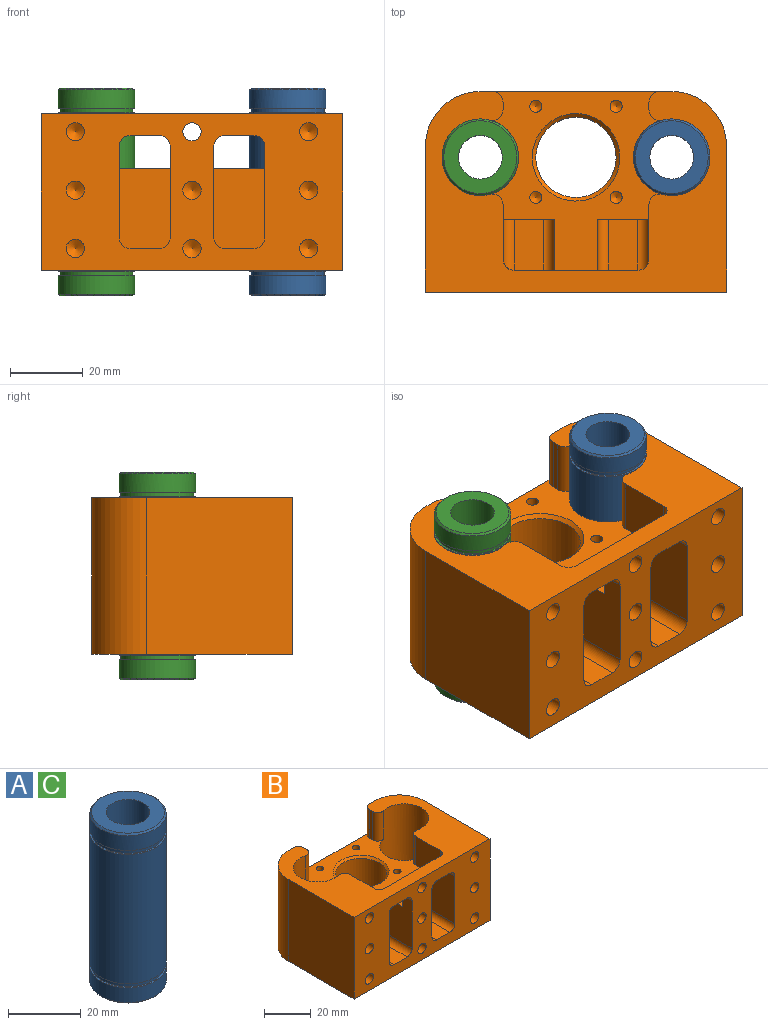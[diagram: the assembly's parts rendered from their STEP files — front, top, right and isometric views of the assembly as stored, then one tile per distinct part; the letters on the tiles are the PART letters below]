
ASSEMBLY  parts=3 mates=2
PART A: 14 faces, bbox 21x21x57 mm
  f0: cylinder r=6mm len=57mm, axis (0,0,1), area 2148.8mm2, adj f1,f7
  f1: plane 20x20mm, normal (0,0,-1), area 201.1mm2, adj f0,f12
  f2: cylinder r=10.5mm len=21mm, axis (0,0,1), area 329.9mm2, adj f3,f12
  f3: plane 21x21mm, normal (0,0,1), area 32.2mm2, adj f2,f4
  f4: cylinder r=10mm len=20mm, axis (0,0,1), area 81.7mm2, adj f3,f5
  f5: plane 21x21mm, normal (0,0,-1), area 32.2mm2, adj f4,f6
  f6: cylinder r=10.5mm len=43.4mm, axis (0,0,1), area 2863.2mm2, adj f5,f11
  f7: plane 20x20mm, normal (0,0,1), area 201.1mm2, adj f0,f13
  f8: cylinder r=10.5mm len=21mm, axis (0,0,-1), area 329.9mm2, adj f9,f13
  f9: plane 21x21mm, normal (0,0,-1), area 32.2mm2, adj f8,f10
  f10: cylinder r=10mm len=20mm, axis (0,0,-1), area 81.7mm2, adj f9,f11
  f11: plane 21x21mm, normal (0,0,1), area 32.2mm2, adj f6,f10
  f12: cone r=10.5mm half-angle=45deg, axis (0,0,1), area 45.5mm2, adj f1,f2
  f13: cone r=10mm half-angle=45deg, axis (0,0,-1), area 45.5mm2, adj f7,f8
PART B: 67 faces, bbox 82.6x55x43 mm
  f0: plane 82.6x43mm, normal (0,-1,0), area 2522.5mm2, adj f5,f6,f7,f9,f12,f14,f35,f37
  f1: plane 49x47.44mm, normal (0,0,1), area 1002.3mm2, adj f2,f4,f8,f9,f10,f13,f14,f15
  f2: plane 34x15mm, normal (0,1,0), area 296.2mm2, adj f1,f3,f6,f26,f48,f51,f53,f58
  f3: cylinder r=3mm len=9mm, axis (0,0,1), area 33.4mm2, adj f2,f6,f9,f55
  f4: plane 52.6x43mm, normal (0,1,0), area 1571.8mm2, adj f1,f6,f7,f11,f16,f29,f30
  f5: plane 43x40mm, normal (-1,0,0), area 1720mm2, adj f0,f6,f7,f11
  f6: plane 82.6x55mm, normal (0,0,1), area 1876.7mm2, adj f0,f2,f3,f4,f5,f8,f9,f10
  f7: plane 82.6x55mm, normal (0,0,-1), area 3373.6mm2, adj f0,f4,f5,f8,f11,f12,f13,f16
  f8: cylinder r=10.5mm len=43mm, axis (0,0,1), area 2418.6mm2, adj f1,f6,f7,f31,f32
  f9: plane 34x23.9mm, normal (1,0,0), area 657.5mm2, adj f0,f1,f3,f6,f31,f54,f55,f56
  f10: plane 15x1.9mm, normal (1,0,0), area 28.5mm2, adj f1,f6,f30,f32
  f11: cylinder r=15mm len=43mm, axis (0,0,1), area 1013.2mm2, adj f4,f5,f6,f7
  f12: plane 43x40mm, normal (1,0,0), area 1720mm2, adj f0,f6,f7,f16
  f13: cylinder r=10.5mm len=43mm, axis (0,0,1), area 2418.6mm2, adj f1,f6,f7,f27,f28
  f14: plane 34x23.9mm, normal (-1,0,0), area 657.5mm2, adj f0,f1,f6,f26,f27,f62,f63,f64
  f15: plane 15x1.9mm, normal (-1,0,0), area 28.5mm2, adj f1,f6,f28,f29
  f16: cylinder r=15mm len=43mm, axis (0,0,1), area 1013.2mm2, adj f4,f6,f7,f12
  f17: cylinder r=11mm len=27mm, axis (0,0,1), area 1866.1mm2, adj f7,f33
  f18: cone r=0mm half-angle=59deg, axis (0,0,1), area 10mm2, adj f19
  f19: cylinder r=1.65mm len=14.1mm, axis (0,0,1), area 146.2mm2, adj f1,f18
  f20: cone r=0mm half-angle=59deg, axis (0,0,1), area 10mm2, adj f21
  f21: cylinder r=1.65mm len=14.1mm, axis (0,0,1), area 146.2mm2, adj f1,f20
  f22: cone r=0mm half-angle=59deg, axis (0,0,1), area 10mm2, adj f23
  f23: cylinder r=1.65mm len=14.1mm, axis (0,0,1), area 146.2mm2, adj f1,f22
  f24: cone r=0mm half-angle=59deg, axis (0,0,1), area 10mm2, adj f25
  f25: cylinder r=1.65mm len=14.1mm, axis (0,0,1), area 146.2mm2, adj f1,f24
  f26: cylinder r=3mm len=9mm, axis (0,0,1), area 33.4mm2, adj f2,f6,f14,f63
  f27: cylinder r=3mm len=15mm, axis (0,0,1), area 81.6mm2, adj f1,f6,f13,f14
  f28: cylinder r=3mm len=15mm, axis (0,0,1), area 81.6mm2, adj f1,f6,f13,f15
  f29: cylinder r=3mm len=15mm, axis (0,0,-1), area 70.7mm2, adj f1,f4,f6,f15
  f30: cylinder r=3mm len=15mm, axis (0,0,-1), area 70.7mm2, adj f1,f4,f6,f10
  f31: cylinder r=3mm len=15mm, axis (0,0,1), area 81.6mm2, adj f1,f6,f8,f9
  f32: cylinder r=3mm len=15mm, axis (0,0,1), area 81.6mm2, adj f1,f6,f8,f10
  f33: cone r=11mm half-angle=45deg, axis (0,0,1), area 102.2mm2, adj f1,f17
  f34: cone r=0mm half-angle=59deg, axis (0,-1,0), area 22.9mm2, adj f35
  f35: cylinder r=2.5mm len=15mm, axis (0,-1,0), area 235.6mm2, adj f0,f34
  f36: cone r=0mm half-angle=59deg, axis (0,-1,0), area 22.9mm2, adj f37
  f37: cylinder r=2.5mm len=15mm, axis (0,-1,0), area 235.6mm2, adj f0,f36
  f38: cone r=0mm half-angle=59deg, axis (0,-1,0), area 22.9mm2, adj f39
  f39: cylinder r=2.5mm len=15mm, axis (0,-1,0), area 235.6mm2, adj f0,f38
  f40: cone r=0mm half-angle=59deg, axis (0,-1,0), area 22.9mm2, adj f41
  f41: cylinder r=2.5mm len=15mm, axis (0,-1,0), area 235.6mm2, adj f0,f40
  f42: cone r=0mm half-angle=59deg, axis (0,-1,0), area 22.9mm2, adj f43
  f43: cylinder r=2.5mm len=15mm, axis (0,-1,0), area 235.6mm2, adj f0,f42
  f44: cone r=0mm half-angle=59deg, axis (0,-1,0), area 22.9mm2, adj f45
  f45: cylinder r=2.5mm len=15mm, axis (0,-1,0), area 235.6mm2, adj f0,f44
  f46: cone r=0mm half-angle=59deg, axis (0,-1,0), area 22.9mm2, adj f47
  f47: cylinder r=2.5mm len=15mm, axis (0,-1,0), area 235.6mm2, adj f0,f46
  f48: cylinder r=2.5mm len=6mm, axis (0,-1,0), area 94.2mm2, adj f0,f2
  f49: cone r=0mm half-angle=59deg, axis (0,-1,0), area 22.9mm2, adj f50
  f50: cylinder r=2.5mm len=15mm, axis (0,-1,0), area 235.6mm2, adj f0,f49
  f51: plane 8x6mm, normal (0,0,-1), area 48mm2, adj f0,f2,f55,f58
  f52: plane 20x8mm, normal (0,0,1), area 160mm2, adj f0,f54,f56,f57
  f53: plane 25x20mm, normal (-1,0,0), area 416mm2, adj f0,f1,f2,f54,f57,f58
  f54: plane 22x14mm, normal (0,-1,0), area 304.1mm2, adj f1,f9,f52,f53,f56,f57
  f55: cylinder r=3mm len=9mm, axis (0,-1,0), area 33.4mm2, adj f0,f3,f9,f51
  f56: cylinder r=3mm len=20mm, axis (0,1,0), area 94.2mm2, adj f0,f9,f52,f54
  f57: cylinder r=3mm len=20mm, axis (0,-1,0), area 94.2mm2, adj f0,f52,f53,f54
  f58: cylinder r=3mm len=6mm, axis (0,1,0), area 28.3mm2, adj f0,f2,f51,f53
  f59: plane 8x6mm, normal (0,0,-1), area 48mm2, adj f0,f2,f63,f66
  f60: plane 25x20mm, normal (1,0,0), area 416mm2, adj f0,f1,f2,f62,f65,f66
  f61: plane 20x8mm, normal (0,0,1), area 160mm2, adj f0,f62,f64,f65
  f62: plane 22x14mm, normal (0,-1,0), area 304.1mm2, adj f1,f14,f60,f61,f64,f65
  f63: cylinder r=3mm len=9mm, axis (0,1,0), area 33.4mm2, adj f0,f14,f26,f59
  f64: cylinder r=3mm len=20mm, axis (0,-1,0), area 94.2mm2, adj f0,f14,f61,f62
  f65: cylinder r=3mm len=20mm, axis (0,-1,0), area 94.2mm2, adj f0,f60,f61,f62
  f66: cylinder r=3mm len=6mm, axis (0,1,0), area 28.3mm2, adj f0,f2,f59,f60
PART C: same geometry as A
PLACE A rot(axis=(0,0,1),0deg) t=(13.88,40.81,29.57)mm
PLACE B t=(-12.37,3.81,8.07)mm fixed
PLACE C t=(-38.62,40.81,29.57)mm
MATE fastened C.f0 <-> B.f8  axis (0,0,1) through (-38.62,40.81,58.07)mm
MATE fastened A.f0 <-> B.f13  axis (0,0,1) through (13.88,40.81,58.07)mm
